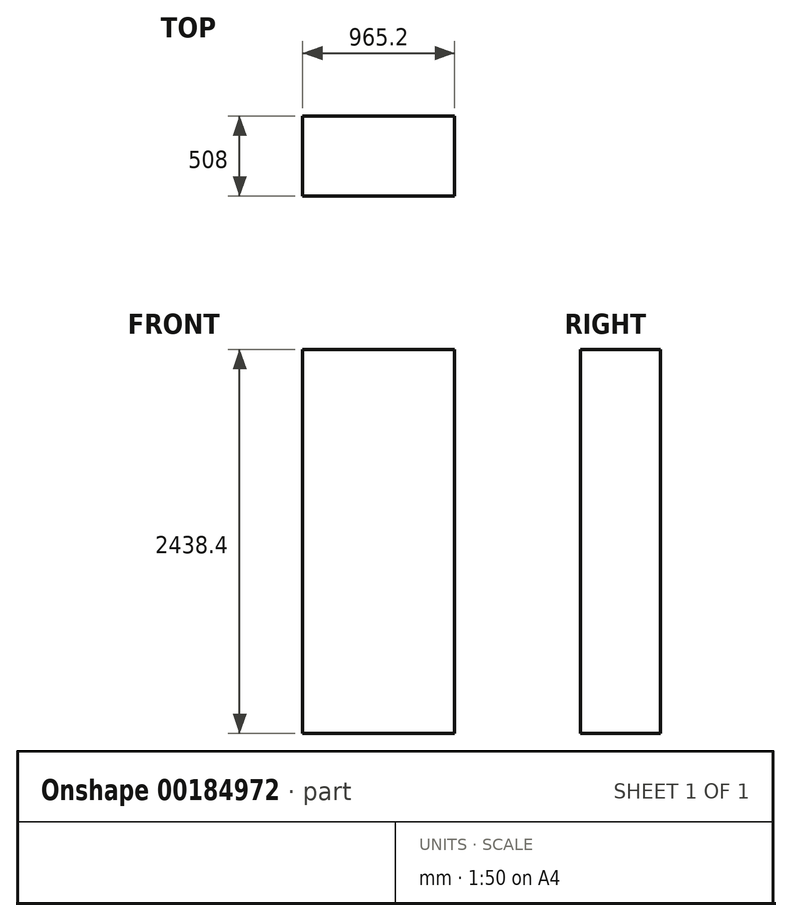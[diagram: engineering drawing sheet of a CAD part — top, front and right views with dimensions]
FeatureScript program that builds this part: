
annotation { "Feature Type Name" : "Feature", "Feature Type Description" : "" }
export const myFeature = defineFeature(function(context is Context, id is Id, definition is map)
    precondition{}
    {
        {
            var Q0;
            Q0=qCreatedBy(makeId("Top.planeOp"),FACE);
            var sketch = newSketch(context, id + "F0", { "sketchPlane" : qUnion([Q0])});
            skLineSegment(sketch, "E0.bottom", {"start": v(482.6, 254) * mm, "end": v(-482.6, 254) * mm});
            skLineSegment(sketch, "E0.top", {"start": v(482.6, -254) * mm, "end": v(-482.6, -254) * mm});
            skLineSegment(sketch, "E0.left", {"start": v(482.6, 254) * mm, "end": v(482.6, -254) * mm});
            skLineSegment(sketch, "E0.right", {"start": v(-482.6, 254) * mm, "end": v(-482.6, -254) * mm});
            skPoint(sketch, "E0.middle", {"position": v(0, 0) * mm});
            skSolve(sketch);
        }
        {
            var Q0;
            Q0=makeQuery(id+"F0.imprint","IMPRINT",FACE,{"disambiguationData":[TD([[makeQuery(id+"F0.imprint","IMPRINT",EDGE,{"derivedFrom":sQuery(id+"F0.wireOp",EDGE,"E0.bottom")}),1.0]])]});
            extrude(context, id + "F1", {"entities" : qUnion([Q0]), "depth" : 2438.4 * mm});
        }
    });
